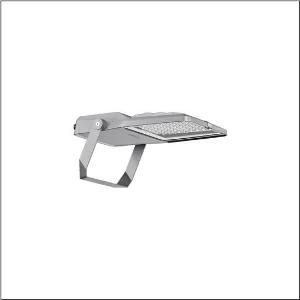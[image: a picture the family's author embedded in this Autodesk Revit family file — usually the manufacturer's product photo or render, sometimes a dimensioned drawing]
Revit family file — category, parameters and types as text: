
# Revit family: floodlight_fl_21_iq_mini___pl33t_5xa7772d5f1a_ae39
name_source: partatom
category: Lighting Fixtures
units: mm (PartAtom-declared; Revit-internal decimal feet)

## family parameters
Cut with Voids When Loaded = No
Host = Face
Light Source = No
Part Type = Normal
Room Calculation Point = No
Round Connector Dimension = Use Diameter
Shared = No

## types (1)
- --- (1 x LED, 16450 lm, 143 W, 4000K)
    Apparent Load = 143 VA
    CIE Flux Codes = 26 75 99 100 100
    Color Rendering = 80
    Color Temperature = 4000K
    Default Elevation = 1800 mm
    Description = Floodlight FL 21 iQ mini, floodlight, primary light control with lens, of PMMA, primary optical cover: protective disc, of toughened safety glass, transparent, light distribution: PL33T, light emission: direct distribution, installation type: surface-mounted, LED, High Power LED, rated luminous flux: 16.450lm, luminous efficacy: 115lm/W, light colour: 840, colour temperature: 4000K, control: Street-Remote, Auto-Match, Temp-Guard, Night-Set, Smart-Wire, Desk-Remote (wireless, voltage-free reading and setting of iQ features in the workshop via application-optimized NFC function/RFID function), optimised constant luminous flux control (CLO 2.0), with terminal, 6-pole, mains connection: 220..240V, AC, 50/60Hz, start of lifetime: 143W, end of service life: 152W, reduction: 61W, luminaire housing, of diecast aluminium, powder-coated, Siteco® metallic grey (DB 702S), corrosivity category C5 mid according to DIN EN ISO 12944, sealing non-destructively replaceable, mounting bracket, of steel, galvanised, powder-coated, Siteco® metallic grey (DB 702S), protection rating (complete): IP66, insulation class (complete): insulation class II (safety insulation), certification: CE, ENEC, VDE, protection symbol: D, impact resistance: IK08, permissible operating ambient temperature: -40..+40°C, permissible operating ambient temperature for outdoor applications: -40..+50°C, standard: DIN EN 12944, LABS conformity tested according to VDMA 24364:2018-05, packaging unit: 1 piece

Light Distribution: PL33T
    Height = 70 mm
    Lamp = 1 x LED
    Lamp Light Flux = 16450 lm
    Lamp Power = 143 W
    Lamp count = 1
    Length = 485 mm
    Luminous efficacy = 115 lm/W
    Manufacturer = Siteco
    ModVariant = No
    Model = 5XA7772D5F1A
    Number of Poles = 1
    OnlyDefault = Yes
    Power Factor = 1
    Product Name = Floodlight FL 21 iQ mini | PL33T
    Product group = floodlight | pylon annexe
    ProductGroupID = 6200
    Protection Class = Protection class II
    Protection Degree = IP 66
    RLX_Detail_Level = 1
    RLX_Emergency_Light_Flux = 0 lm
    RLX_Emergency_Type = 0
    RLX_Emergency_Type_DB = No
    RlxData = <blob elided: 96413 chars, md5=ea5864ee>
    Socket = socket
    Standby Power = 0 W
    System Light Flux = 16450 lm
    System Power = 143 W
    Type Comments = factory setting: luminous flux: 100 % | dim-lin: 254 | 730 mA
    Type Image = l_1006845.jpg
    URL = http://relux.com
    VarID = @adj_081225
    Voltage = 0 V
    Weight = 0.00 kg
    Width = 337 mm

## geometry (parser evidence)
native form markers: Blend x4, Sweep x12
no freeform markers — native parametric forms only
